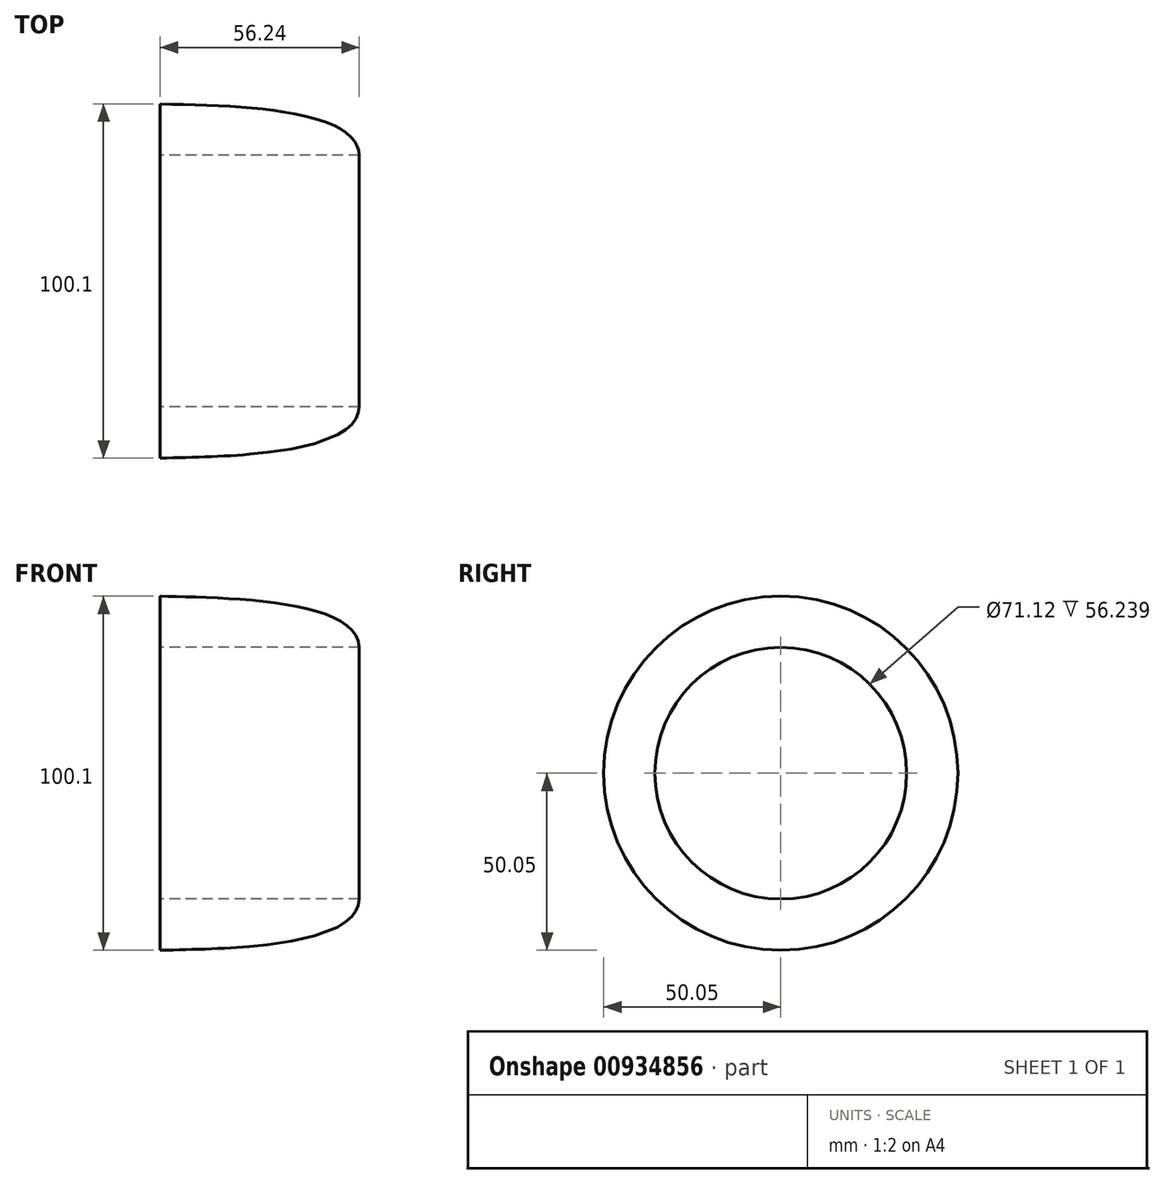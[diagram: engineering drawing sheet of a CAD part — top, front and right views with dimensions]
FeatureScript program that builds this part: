
annotation { "Feature Type Name" : "Feature", "Feature Type Description" : "" }
export const myFeature = defineFeature(function(context is Context, id is Id, definition is map)
    precondition{}
    {
        {
            var Q0;
            Q0=qCreatedBy(makeId("Front.planeOp"),FACE);
            var sketch = newSketch(context, id + "F0", { "sketchPlane" : qUnion([Q0])});
            skLineSegment(sketch, "E0", {"start": v(0, 0) * mm, "end": v(0, 50.05) * mm});
            skLineSegment(sketch, "E1", {"start": v(0, 0) * mm, "end": v(56.24, 0) * mm});
            skLineSegment(sketch, "E2", {"start": v(56.24, 0) * mm, "end": v(56.24, 35.48) * mm});
            skFitSpline(sketch, "E3", {"points": [v(0, 50.05) * mm, v(56.24, 35.48) * mm], "startDerivative": vector(47.39, -1.48) * mm, "endDerivative": vector(0.74, -42.95) * mm});
            skSolve(sketch);
        }
        {
            var Q0;
            Q0=makeQuery(id+"F0.imprint","IMPRINT",FACE,{"disambiguationData":[TD([[makeQuery(id+"F0.imprint","IMPRINT",EDGE,{"derivedFrom":sQuery(id+"F0.wireOp",EDGE,"E0")}),-1.0]])]});
            var Q1;
            Q1=sQuery(id+"F0.wireOp",EDGE,"E1");
            revolve(context, id + "F1", {"surfaceOperationType" : NewSurfaceOperationType.NEW, "entities" : qUnion([Q0]), "axis" : qUnion([Q1]), "revolveType" : RevolveType.FULL});
        }
        {
            var Q0;
            Q0=qCreatedBy(makeId("Right.planeOp"),FACE);
            var sketch = newSketch(context, id + "F2", { "sketchPlane" : qUnion([Q0])});
            skPoint(sketch, "E4", {"position": v(0, 0) * mm});
            skSolve(sketch);
        }
        {
            var Q0;
            Q0=sQuery(id+"F2.wireOp",VERTEX,"E4");
            var Q1;
            Q1=makeQuery(id+"F1.opRevolve","SWEPT_BODY",BODY,{"disambiguationData":[OSD([sQuery(id+"F0.wireOp",EDGE,"E0"),sQuery(id+"F0.wireOp",EDGE,"E1"),sQuery(id+"F0.wireOp",EDGE,"E2"),sQuery(id+"F0.wireOp",EDGE,"E3")])]});
            hole(context, id + "F3", {"style" : HoleStyle.SIMPLE, "endStyle" : HoleEndStyle.THROUGH, "oppositeDirection" : true, "holeDiameter" : 71.12 * mm, "majorDiameter" : 6.35 * mm, "isTappedThrough" : true, "tappedDepth" : 12.7 * mm, "tapClearance" : 3, "locations" : qUnion([Q0]), "scope" : qUnion([Q1])});
        }
    });
